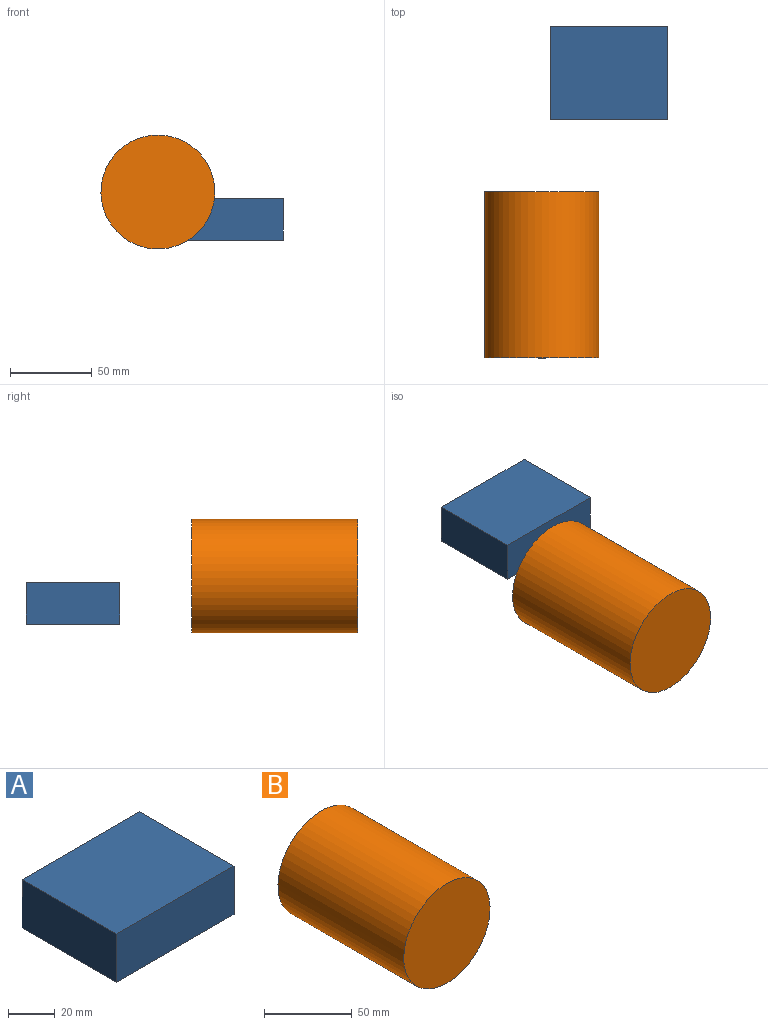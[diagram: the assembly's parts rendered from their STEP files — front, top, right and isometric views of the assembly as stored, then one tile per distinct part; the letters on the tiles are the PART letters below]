
ASSEMBLY  parts=2 mates=1
PART A: 6 faces, bbox 71.6x57.2x25.4 mm
  f0: plane 71.58x25.4mm, normal (0,-1,0), area 1818.1mm2, adj f1,f3,f4,f5
  f1: plane 57.18x25.4mm, normal (1,0,0), area 1452.4mm2, adj f0,f2,f4,f5
  f2: plane 71.58x25.4mm, normal (0,1,0), area 1818.1mm2, adj f1,f3,f4,f5
  f3: plane 57.18x25.4mm, normal (-1,0,0), area 1452.4mm2, adj f0,f2,f4,f5
  f4: plane 71.58x57.18mm, normal (0,0,1), area 4092.8mm2, adj f0,f1,f2,f3
  f5: plane 71.58x57.18mm, normal (0,0,-1), area 4092.8mm2, adj f0,f1,f2,f3
PART B: 3 faces, bbox 69.7x101.6x69.7 mm
  f0: cylinder r=34.84mm len=101.6mm, axis (0,1,0), area 22239.7mm2, adj f1,f2
  f1: plane 69.68x69.68mm, normal (0,-1,0), area 3813mm2, adj f0
  f2: plane 69.68x69.68mm, normal (0,1,0), area 3813mm2, adj f0
PLACE A t=(-17.58,-2.61,4.88)mm fixed
PLACE B rot(axis=(1,0,0),180deg) t=(-63.67,-175.92,34.28)mm
MATE slider B.f1 <-> A.f0  axis (0,1,0) through (-58.67,-74.32,30.28)mm
